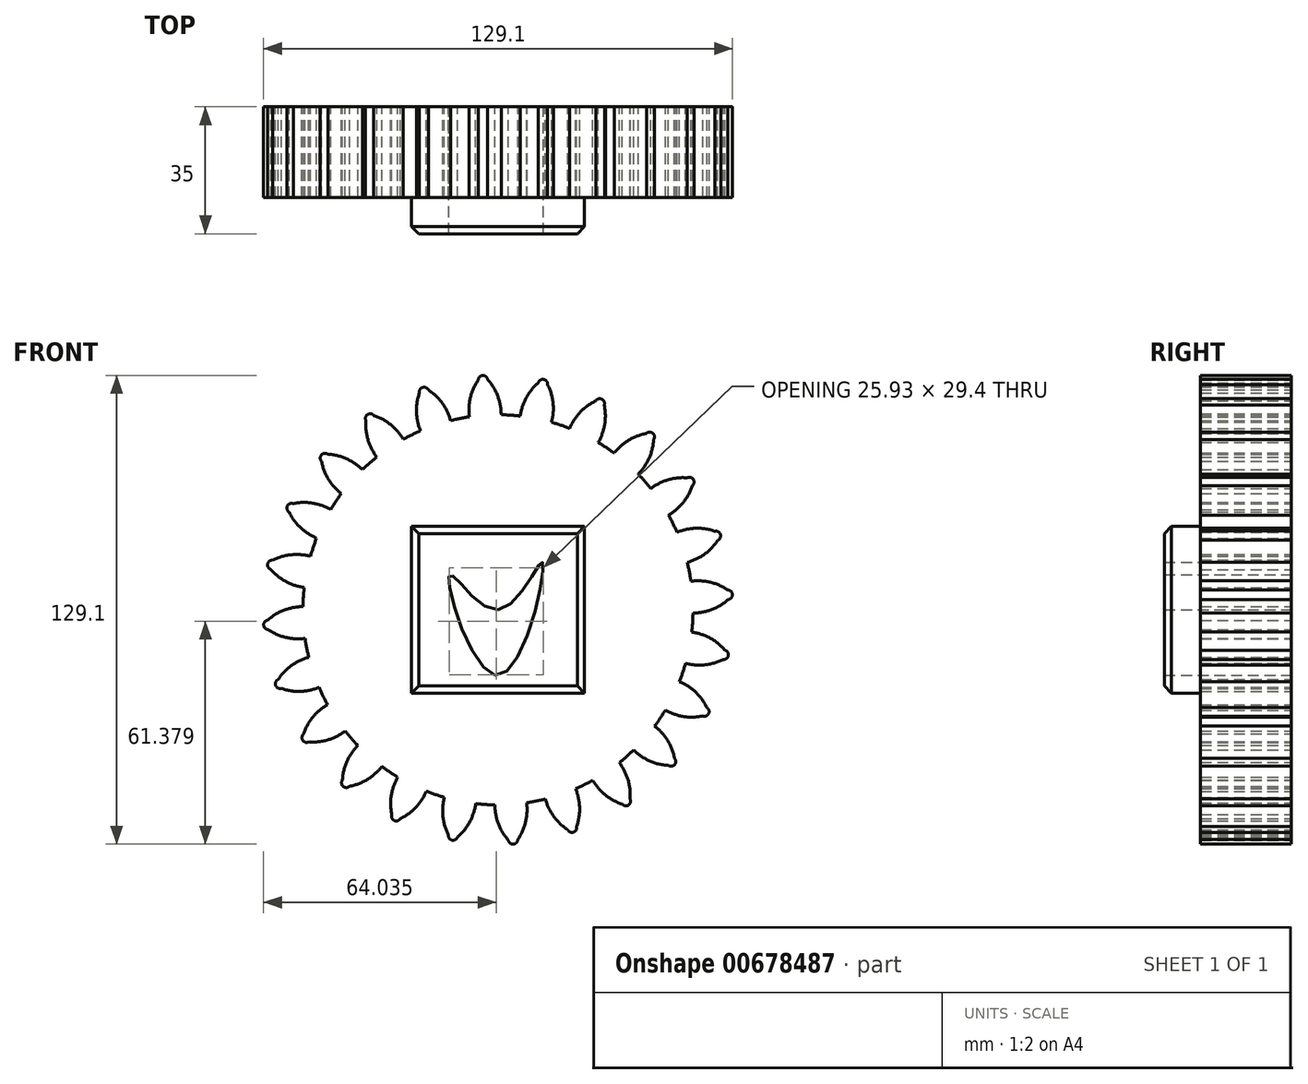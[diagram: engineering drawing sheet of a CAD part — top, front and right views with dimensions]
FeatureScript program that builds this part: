
annotation { "Feature Type Name" : "Feature", "Feature Type Description" : "" }
export const myFeature = defineFeature(function(context is Context, id is Id, definition is map)
    precondition{}
    {
        {
            var Q0;
            Q0=qCreatedBy(makeId("Front.planeOp"),FACE);
            var sketch = newSketch(context, id + "F0", { "sketchPlane" : qUnion([Q0])});
            skCircle(sketch, "E0", {"center": v(0, 0) * mm, "radius": 53.72 * mm});
            skCircle(sketch, "E1", {"center": v(0, 0) * mm, "radius": 58.67 * mm, "construction": true});
            skCircle(sketch, "E2", {"center": v(0, 0) * mm, "radius": 63.5 * mm, "construction": true});
            skLineSegment(sketch, "E3", {"start": v(0, 0) * mm, "end": v(0, 72.67) * mm, "construction": true});
            skLineSegment(sketch, "E4", {"start": v(0, 0) * mm, "end": v(-5.05, 77.02) * mm, "construction": true});
            skLineSegment(sketch, "E5", {"start": v(0, 58.67) * mm, "end": v(-57.47, 58.67) * mm, "construction": true});
            skLineSegment(sketch, "E6", {"start": v(0, 58.67) * mm, "end": v(-61.26, 36.38) * mm, "construction": true});
            skCircle(sketch, "E7", {"center": v(0, 0) * mm, "radius": 55.14 * mm, "construction": true});
            skCircle(sketch, "E8", {"center": v(0, 58.67) * mm, "radius": 14.6 * mm, "construction": true});
            skCircle(sketch, "E9", {"center": v(-13.72, 53.68) * mm, "radius": 14.6 * mm, "construction": true});
            skArc(sketch, "E10", {"start": v(0, 58.67) * mm, "mid": v(-1.19, 61.2) * mm, "end": v(-2.86, 63.44) * mm});
            skArc(sketch, "E11", {"start": v(0.88, 53.71) * mm, "mid": v(0.64, 56.23) * mm, "end": v(0, 58.67) * mm});
            skArc(sketch, "E12.MirrorCS", {"start": v(-7.66, 58.17) * mm, "mid": v(-6.8, 60.83) * mm, "end": v(-5.45, 63.27) * mm});
            skArc(sketch, "E13.MirrorCS", {"start": v(-7.88, 53.14) * mm, "mid": v(-7.98, 55.66) * mm, "end": v(-7.66, 58.17) * mm});
            skArc(sketch, "E14", {"start": v(-2.86, 63.44) * mm, "mid": v(-4.23, 64.55) * mm, "end": v(-5.45, 63.27) * mm});
            skLineSegment(sketch, "E15.bottom", {"start": v(-23.82, 23) * mm, "end": v(23.82, 23) * mm});
            skLineSegment(sketch, "E15.top", {"start": v(-23.82, -23) * mm, "end": v(23.82, -23) * mm});
            skLineSegment(sketch, "E15.left", {"start": v(-23.82, 23) * mm, "end": v(-23.82, -23) * mm});
            skLineSegment(sketch, "E15.right", {"start": v(23.82, 23) * mm, "end": v(23.82, -23) * mm});
            skFitSpline(sketch, "E16", {"points": [v(0, 0) * mm, v(12.25, 13.08) * mm, v(0, -18.04) * mm, v(-13.35, 9.5) * mm, v(0, 0) * mm]});
            skSolve(sketch);
        }
        {
            var Q0;
            {var subQ0=sQuery(id+"F0.wireOp",EDGE,"E0");var subQ1=makeQuery(id+"F0.imprint","INTERSECT",VERTEX,{"derivedFrom":[subQ0,sQuery(id+"F0.wireOp",EDGE,"E11")]});Q0=makeQuery(id+"F0.imprint","IMPRINT",FACE,{"disambiguationData":[TD([[makeQuery(id+"F0.imprint","IMPRINT",EDGE,{"disambiguationData":[TD([[subQ1,-1.0]])],"derivedFrom":subQ0}),1.0]])]});}
            var Q1;
            Q1=makeQuery(id+"F0.imprint","IMPRINT",FACE,{"disambiguationData":[TD([[makeQuery(id+"F0.imprint","IMPRINT",EDGE,{"derivedFrom":sQuery(id+"F0.wireOp",EDGE,"E10")}),1.0]])]});
            extrude(context, id + "F1", {"entities" : qUnion([Q0, Q1]), "depth" : 25 * mm, "offsetDistance" : 25 * mm});
        }
        {
            var Q0;
            Q0=makeQuery(id+"F1.opExtrude","SWEPT_BODY",BODY,{"disambiguationData":[OSD([sQuery(id+"F0.wireOp",EDGE,"E0"),sQuery(id+"F0.wireOp",EDGE,"E10"),sQuery(id+"F0.wireOp",EDGE,"E11"),sQuery(id+"F0.wireOp",EDGE,"E12.MirrorCS"),sQuery(id+"F0.wireOp",EDGE,"E13.MirrorCS"),sQuery(id+"F0.wireOp",EDGE,"E14")])]});
            var Q1;
            Q1=makeQuery(id+"F1.opExtrude","SWEPT_FACE",FACE,{"disambiguationData":[OSD([sQuery(id+"F0.wireOp",EDGE,"E0")])]});
            circularPattern(context, id + "F2", {"entities" : qUnion([Q0]), "axis" : qUnion([Q1]), "angle" : 360 * degree, "instanceCount" : 24, "equalSpace" : true});
        }
        {
            var Q0;
            Q0=makeQuery(id+"F0.imprint","IMPRINT",FACE,{"disambiguationData":[TD([[makeQuery(id+"F0.imprint","IMPRINT",EDGE,{"derivedFrom":sQuery(id+"F0.wireOp",EDGE,"E15.bottom")}),-1.0]])]});
            extrude(context, id + "F3", {"entities" : qUnion([Q0]), "operationType" : NewBodyOperationType.ADD, "depth" : 35 * mm, "offsetDistance" : 25 * mm});
        }
        {
            var Q0;
            Q0=makeQuery(id+"F3.opExtrude","CAP_EDGE",EDGE,{"disambiguationData":[OSD([sQuery(id+"F0.wireOp",EDGE,"E15.bottom")])],"isStart":false});
            var Q1;
            Q1=makeQuery(id+"F3.opExtrude","CAP_EDGE",EDGE,{"disambiguationData":[OSD([sQuery(id+"F0.wireOp",EDGE,"E15.left")])],"isStart":false});
            var Q2;
            Q2=makeQuery(id+"F3.opExtrude","CAP_EDGE",EDGE,{"disambiguationData":[OSD([sQuery(id+"F0.wireOp",EDGE,"E15.top")])],"isStart":false});
            var Q3;
            Q3=makeQuery(id+"F3.opExtrude","CAP_EDGE",EDGE,{"disambiguationData":[OSD([sQuery(id+"F0.wireOp",EDGE,"E15.right")])],"isStart":false});
            chamfer(context, id + "F4", {"entities" : qUnion([Q0, Q1, Q2, Q3]), "width" : 2 * mm, "tangentPropagation" : true});
        }
    });
